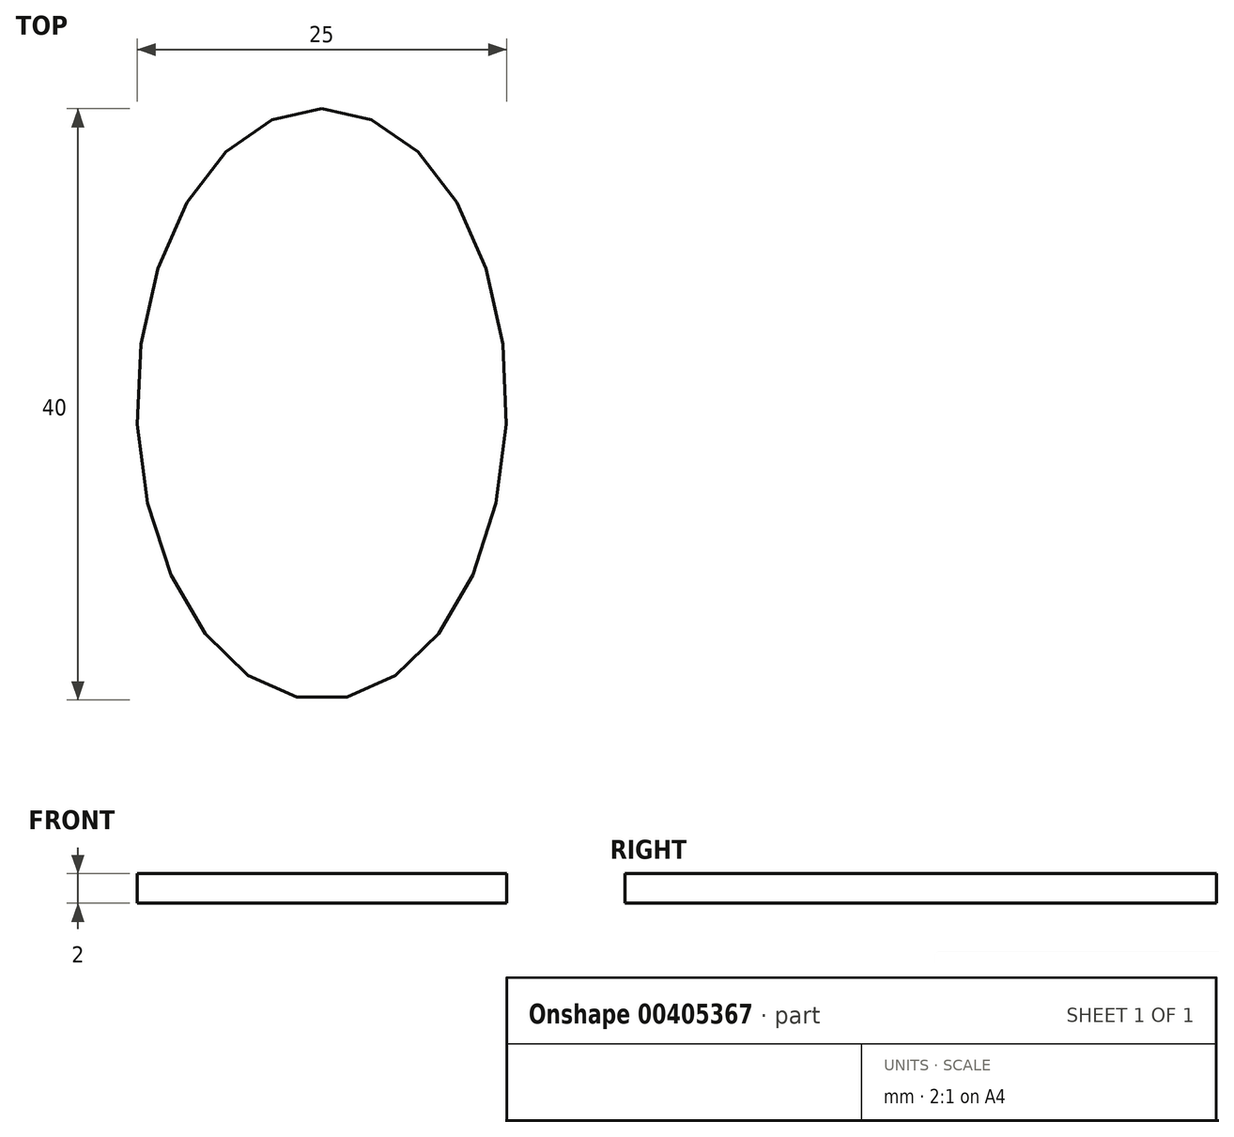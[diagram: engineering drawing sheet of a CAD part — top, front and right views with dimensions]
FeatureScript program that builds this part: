
annotation { "Feature Type Name" : "Feature", "Feature Type Description" : "" }
export const myFeature = defineFeature(function(context is Context, id is Id, definition is map)
    precondition{}
    {
        {
            var Q0;
            Q0=qCreatedBy(makeId("Top.planeOp"),FACE);
            var sketch = newSketch(context, id + "F0", { "sketchPlane" : qUnion([Q0])});
            skEllipse(sketch, "E0", {"center": v(0, 0) * mm, "majorRadius": 20 * mm, "minorRadius": 12.5 * mm, "majorAxis": v(0, 1)});
            skSolve(sketch);
        }
        {
            var Q0;
            Q0=makeQuery(id+"F0.imprint","IMPRINT",FACE,{"disambiguationData":[TD([[makeQuery(id+"F0.imprint","IMPRINT",EDGE,{"derivedFrom":sQuery(id+"F0.wireOp",EDGE,"E0")}),1.0]])]});
            extrude(context, id + "F1", {"entities" : qUnion([Q0]), "depth" : 2 * mm});
        }
    });
